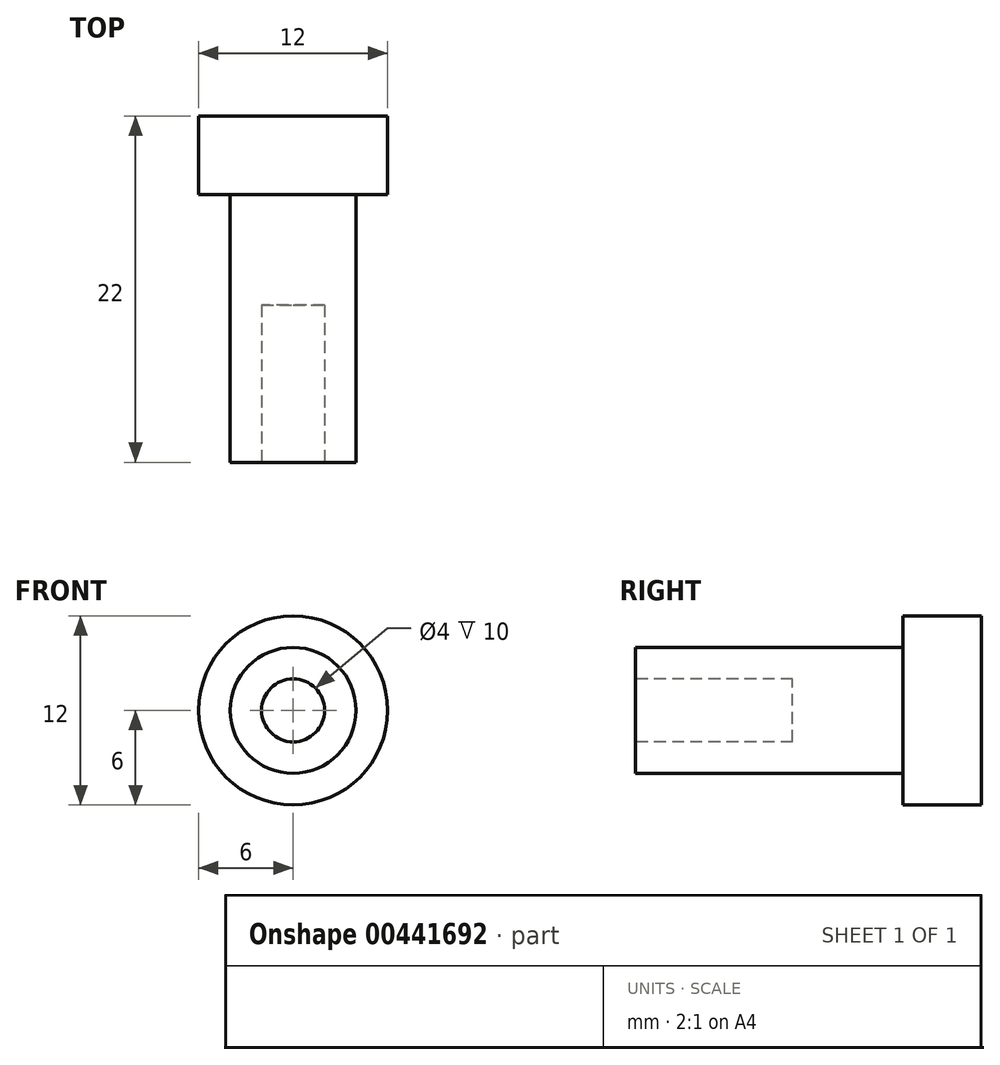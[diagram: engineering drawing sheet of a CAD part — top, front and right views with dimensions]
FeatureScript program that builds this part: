
annotation { "Feature Type Name" : "Feature", "Feature Type Description" : "" }
export const myFeature = defineFeature(function(context is Context, id is Id, definition is map)
    precondition{}
    {
        {
            var Q0;
            Q0=qCreatedBy(makeId("Front.planeOp"),FACE);
            var sketch = newSketch(context, id + "F0", { "sketchPlane" : qUnion([Q0])});
            skCircle(sketch, "E0", {"center": v(0, 0) * mm, "radius": 6 * mm});
            skSolve(sketch);
        }
        {
            var Q0;
            Q0 = qSketchRegion(id + "F0", true);
            extrude(context, id + "F1", {"entities" : qUnion([Q0]), "endBound" : BoundingType.SYMMETRIC, "depth" : 5 * mm});
        }
        {
            var Q0;
            Q0=makeQuery(id+"F1.opExtrude","CAP_FACE",FACE,{"disambiguationData":[OSD([sQuery(id+"F0.wireOp",EDGE,"E0")])],"isStart":false});
            var sketch = newSketch(context, id + "F2", { "sketchPlane" : qUnion([Q0])});
            skCircle(sketch, "E1", {"center": v(0, 0) * mm, "radius": 4 * mm});
            skSolve(sketch);
        }
        {
            var Q0;
            Q0 = qSketchRegion(id + "F2", true);
            extrude(context, id + "F3", {"entities" : qUnion([Q0]), "operationType" : NewBodyOperationType.ADD, "depth" : 17 * mm, "offsetDistance" : 25 * mm});
        }
        {
            var Q0;
            Q0=makeQuery(id+"F3.opExtrude","CAP_FACE",FACE,{"disambiguationData":[OSD([sQuery(id+"F2.wireOp",EDGE,"E1")])],"isStart":false});
            var sketch = newSketch(context, id + "F4", { "sketchPlane" : qUnion([Q0])});
            skCircle(sketch, "E2", {"center": v(0, 0) * mm, "radius": 2 * mm});
            skSolve(sketch);
        }
        {
            var Q0;
            Q0 = qSketchRegion(id + "F4", true);
            extrude(context, id + "F5", {"entities" : qUnion([Q0]), "operationType" : NewBodyOperationType.REMOVE, "oppositeDirection" : true, "depth" : 10 * mm});
        }
    });
